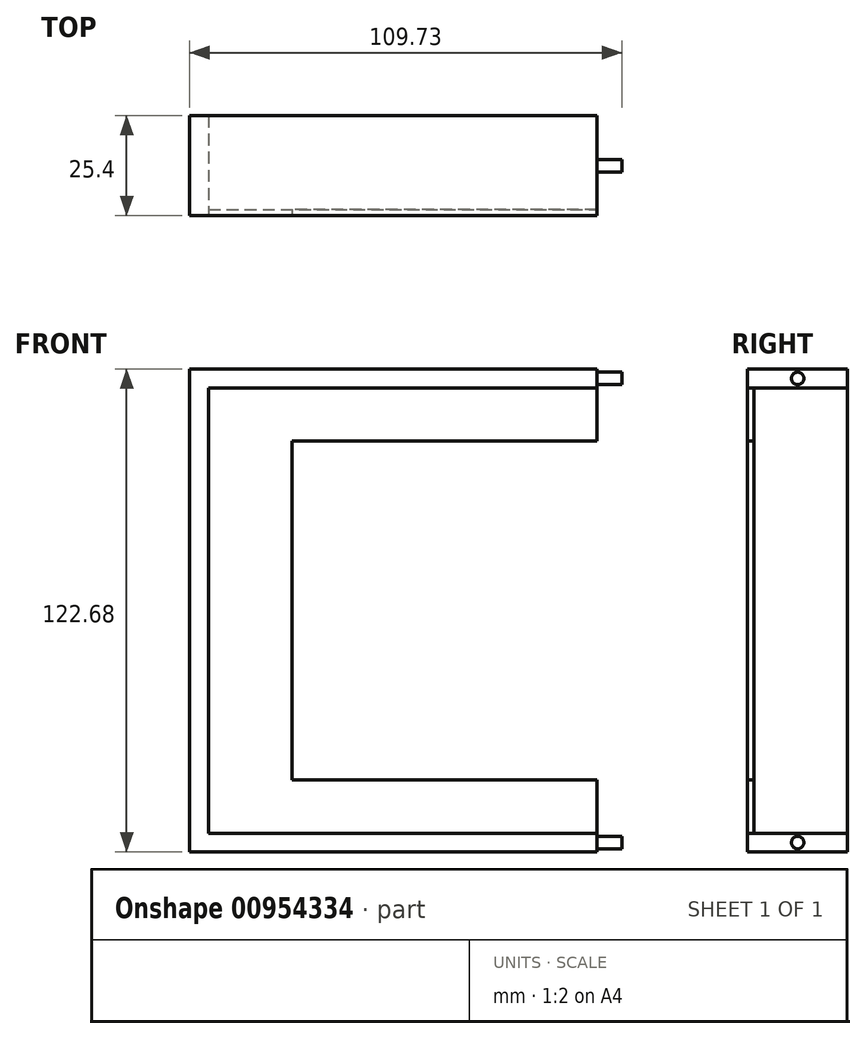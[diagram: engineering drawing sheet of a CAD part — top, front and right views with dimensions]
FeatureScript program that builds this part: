
annotation { "Feature Type Name" : "Feature", "Feature Type Description" : "" }
export const myFeature = defineFeature(function(context is Context, id is Id, definition is map)
    precondition{}
    {
        {
            var Q0;
            Q0=qCreatedBy(makeId("Front.planeOp"),FACE);
            var sketch = newSketch(context, id + "F0", { "sketchPlane" : qUnion([Q0])});
            skLineSegment(sketch, "E0.bottom", {"start": v(77.47, 43.05) * mm, "end": v(-77.47, 43.05) * mm});
            skLineSegment(sketch, "E0.top", {"start": v(77.47, -43.05) * mm, "end": v(-77.47, -43.05) * mm});
            skLineSegment(sketch, "E0.left", {"start": v(77.47, 43.05) * mm, "end": v(77.47, -43.05) * mm});
            skLineSegment(sketch, "E0.right", {"start": v(-77.47, 43.05) * mm, "end": v(-77.47, -43.05) * mm});
            skPoint(sketch, "E0.middle", {"position": v(0, 0) * mm});
            skLineSegment(sketch, "E1.bottom", {"start": v(-97.03, 55) * mm, "end": v(97.03, 55) * mm});
            skLineSegment(sketch, "E1.top", {"start": v(-97.03, -55) * mm, "end": v(97.03, -55) * mm});
            skLineSegment(sketch, "E1.left", {"start": v(-97.03, 55) * mm, "end": v(-97.03, -55) * mm});
            skLineSegment(sketch, "E1.right", {"start": v(97.03, 55) * mm, "end": v(97.03, -55) * mm});
            skLineSegment(sketch, "E2.0", {"start": v(-98.62, 56.58) * mm, "end": v(-98.62, -56.58) * mm});
            skLineSegment(sketch, "E2.1", {"start": v(-98.62, 56.58) * mm, "end": v(98.62, 56.58) * mm});
            skLineSegment(sketch, "E2.2", {"start": v(98.62, 56.58) * mm, "end": v(98.62, -56.58) * mm});
            skLineSegment(sketch, "E2.3", {"start": v(-98.62, -56.58) * mm, "end": v(98.62, -56.58) * mm});
            skLineSegment(sketch, "E3.0", {"start": v(-103.38, 61.34) * mm, "end": v(-103.38, -61.34) * mm});
            skLineSegment(sketch, "E3.1", {"start": v(-103.38, 61.34) * mm, "end": v(103.38, 61.34) * mm});
            skLineSegment(sketch, "E3.2", {"start": v(103.38, 61.34) * mm, "end": v(103.38, -61.34) * mm});
            skLineSegment(sketch, "E3.3", {"start": v(-103.38, -61.34) * mm, "end": v(103.38, -61.34) * mm});
            skLineSegment(sketch, "E4", {"start": v(0, 43.05) * mm, "end": v(0, 61.34) * mm});
            skLineSegment(sketch, "E5", {"start": v(0, -43.05) * mm, "end": v(0, -61.34) * mm});
            skSolve(sketch);
        }
        {
            var Q0;
            {var subQ0=sQuery(id+"F0.wireOp",EDGE,"E0.right");Q0=makeQuery(id+"F0.imprint","IMPRINT",FACE,{"disambiguationData":[TD([[makeQuery(id+"F0.imprint","IMPRINT",EDGE,{"derivedFrom":subQ0}),-1.0]])]});}
            var Q1;
            {var subQ1=sQuery(id+"F0.wireOp",EDGE,"E1.left");Q1=makeQuery(id+"F0.imprint","IMPRINT",FACE,{"disambiguationData":[TD([[makeQuery(id+"F0.imprint","IMPRINT",EDGE,{"derivedFrom":subQ1}),-1.0]])]});}
            extrude(context, id + "F1", {"entities" : qUnion([Q0, Q1]), "oppositeDirection" : true, "depth" : 1.59 * mm, "offsetDistance" : 25.4 * mm});
        }
        {
            var Q0;
            Q0=makeQuery(id+"F0.imprint","IMPRINT",FACE,{"disambiguationData":[TD([[makeQuery(id+"F0.imprint","IMPRINT",EDGE,{"derivedFrom":sQuery(id+"F0.wireOp",EDGE,"E2.0")}),-1.0]])]});
            extrude(context, id + "F2", {"entities" : qUnion([Q0]), "oppositeDirection" : true, "depth" : 25.4 * mm, "offsetDistance" : 25.4 * mm});
        }
        {
            var Q0;
            Q0=makeQuery(id+"F2.opExtrude","SWEPT_FACE",FACE,{"disambiguationData":[OSD([sQuery(id+"F0.wireOp",EDGE,"E5")])]});
            var sketch = newSketch(context, id + "F3", { "sketchPlane" : qUnion([Q0])});
            skCircle(sketch, "E6", {"center": v(12.7, -58.96) * mm, "radius": 1.59 * mm});
            skSolve(sketch);
        }
        {
            var Q0;
            Q0=makeQuery(id+"F3.imprint","IMPRINT",FACE,{"disambiguationData":[TD([[makeQuery(id+"F3.imprint","IMPRINT",EDGE,{"derivedFrom":sQuery(id+"F3.wireOp",EDGE,"E6")}),1.0]])]});
            extrude(context, id + "F4", {"entities" : qUnion([Q0]), "operationType" : NewBodyOperationType.ADD, "depth" : 6.35 * mm, "offsetDistance" : 25.4 * mm});
        }
        {
            var Q0;
            Q0=makeQuery(id+"F2.opExtrude","SWEPT_FACE",FACE,{"disambiguationData":[OSD([sQuery(id+"F0.wireOp",EDGE,"E4")])]});
            var sketch = newSketch(context, id + "F5", { "sketchPlane" : qUnion([Q0])});
            skCircle(sketch, "E7", {"center": v(12.7, 58.96) * mm, "radius": 1.59 * mm});
            skSolve(sketch);
        }
        {
            var Q0;
            Q0=makeQuery(id+"F5.imprint","IMPRINT",FACE,{"disambiguationData":[TD([[makeQuery(id+"F5.imprint","IMPRINT",EDGE,{"derivedFrom":sQuery(id+"F5.wireOp",EDGE,"E7")}),1.0]])]});
            extrude(context, id + "F6", {"entities" : qUnion([Q0]), "operationType" : NewBodyOperationType.ADD, "depth" : 6.35 * mm, "offsetDistance" : 25.4 * mm});
        }
    });
